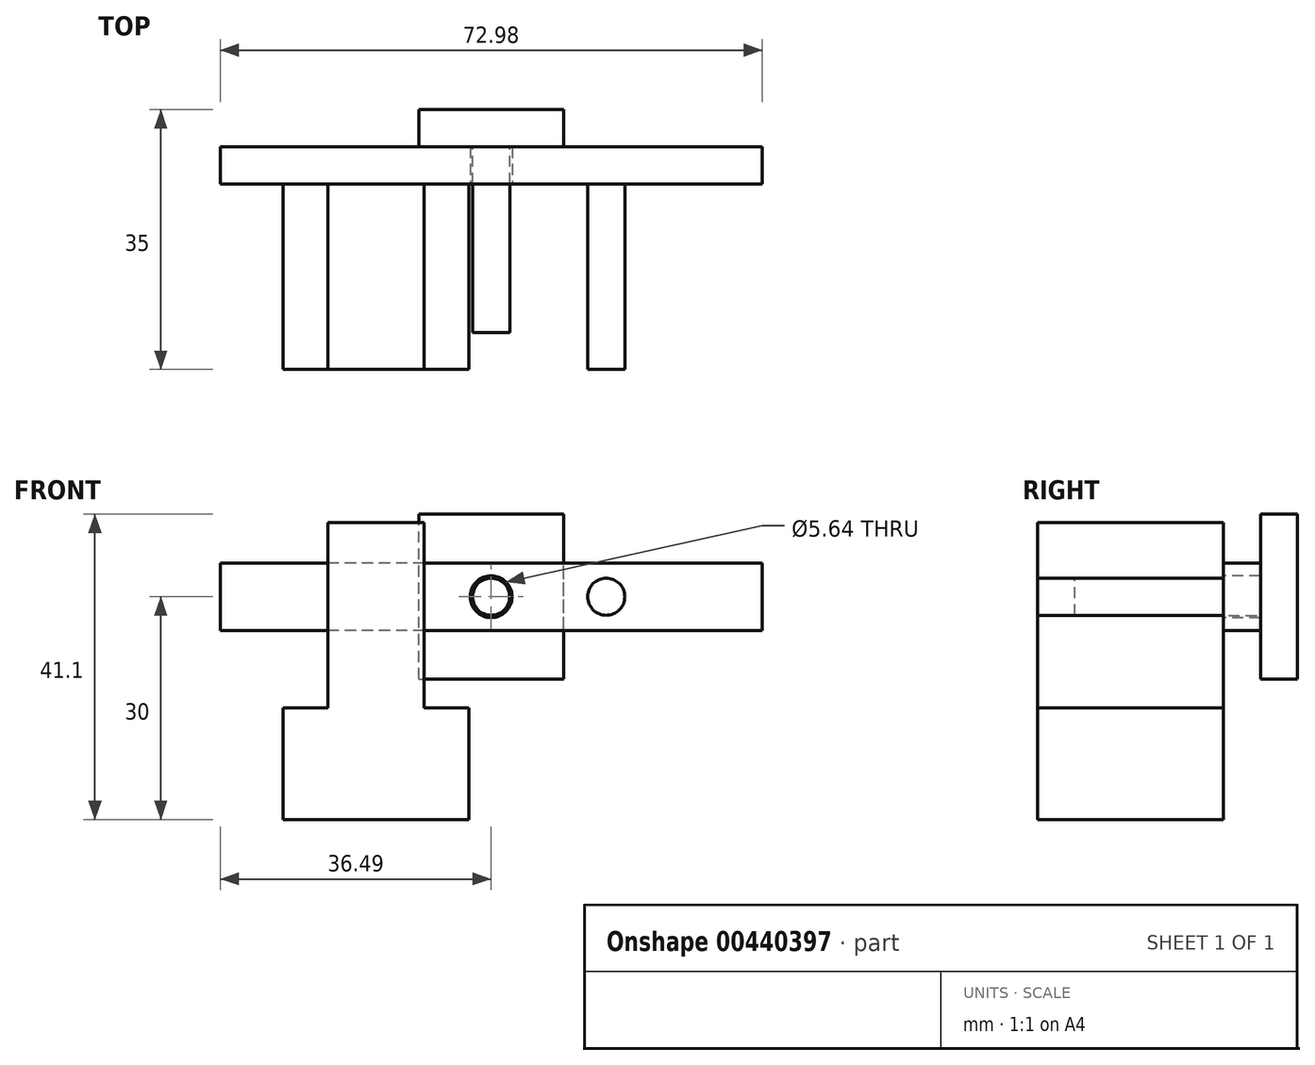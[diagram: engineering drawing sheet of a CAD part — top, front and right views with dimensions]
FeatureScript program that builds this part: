
annotation { "Feature Type Name" : "Feature", "Feature Type Description" : "" }
export const myFeature = defineFeature(function(context is Context, id is Id, definition is map)
    precondition{}
    {
        {
            var Q0;
            Q0=qCreatedBy(makeId("Front.planeOp"),FACE);
            var sketch = newSketch(context, id + "F0", { "sketchPlane" : qUnion([Q0])});
            skLineSegment(sketch, "E0.bottom", {"start": v(-28, 0) * mm, "end": v(-3, 0) * mm});
            skLineSegment(sketch, "E0.top", {"start": v(-28, -30) * mm, "end": v(-3, -30) * mm});
            skLineSegment(sketch, "E0.left", {"start": v(-28, 0) * mm, "end": v(-28, -30) * mm});
            skLineSegment(sketch, "E0.right", {"start": v(-3, 0) * mm, "end": v(-3, -30) * mm});
            skSolve(sketch);
        }
        {
            var Q0;
            Q0 = qSketchRegion(id + "F0", true);
            extrude(context, id + "F1", {"entities" : qUnion([Q0]), "depth" : 25 * mm});
        }
        {
            var Q0;
            Q0=makeQuery(id+"F1.opExtrude","SWEPT_FACE",FACE,{"disambiguationData":[OSD([sQuery(id+"F0.wireOp",EDGE,"E0.bottom")])]});
            extrude(context, id + "F2", {"entities" : qUnion([Q0]), "operationType" : NewBodyOperationType.ADD, "depth" : 10 * mm});
        }
        {
            var Q0;
            {var subQ0=sQuery(id+"F0.wireOp",EDGE,"E0.bottom");Q0=makeQuery(id+"F2.boolean.opBoolean","MERGE",FACE,{"derivedFrom":[makeQuery(id+"F1.opExtrude","CAP_FACE",FACE,{"disambiguationData":[OSD([subQ0,sQuery(id+"F0.wireOp",EDGE,"E0.top"),sQuery(id+"F0.wireOp",EDGE,"E0.left"),sQuery(id+"F0.wireOp",EDGE,"E0.right")])],"isStart":false}),makeQuery(id+"F2.opExtrude","SWEPT_FACE",FACE,{"disambiguationData":[OSD([subQ0]),TDD([makeQuery(id+"F1.opExtrude","CAP_EDGE",EDGE,{"disambiguationData":[OSD([subQ0])],"isStart":false})])]})]});}
            var sketch = newSketch(context, id + "F3", { "sketchPlane" : qUnion([Q0])});
            skLineSegment(sketch, "E1", {"start": v(-15.5, 10) * mm, "end": v(-15.5, -13.59) * mm, "construction": true});
            skCircle(sketch, "E2", {"center": v(-15.5, 0) * mm, "radius": 2.5 * mm});
            skSolve(sketch);
        }
        {
            var Q0;
            Q0 = qSketchRegion(id + "F3", true);
            extrude(context, id + "F4", {"entities" : qUnion([Q0]), "operationType" : NewBodyOperationType.REMOVE, "oppositeDirection" : true, "depth" : 25 * mm});
        }
        {
            var Q0;
            Q0=qCreatedBy(makeId("Front.planeOp"),FACE);
            var sketch = newSketch(context, id + "F5", { "sketchPlane" : qUnion([Q0])});
            skLineSegment(sketch, "E3.bottom", {"start": v(36.49, -4.53) * mm, "end": v(-36.49, -4.53) * mm});
            skLineSegment(sketch, "E3.top", {"start": v(36.49, 4.53) * mm, "end": v(-36.49, 4.53) * mm});
            skLineSegment(sketch, "E3.left", {"start": v(36.49, -4.53) * mm, "end": v(36.49, 4.53) * mm});
            skLineSegment(sketch, "E3.right", {"start": v(-36.49, -4.53) * mm, "end": v(-36.49, 4.53) * mm});
            skPoint(sketch, "E3.middle", {"position": v(0, 0) * mm});
            skSolve(sketch);
        }
        {
            var Q0;
            Q0 = qSketchRegion(id + "F5", true);
            extrude(context, id + "F6", {"entities" : qUnion([Q0]), "oppositeDirection" : true, "depth" : 5 * mm});
        }
        {
            var Q0;
            Q0=makeQuery(id+"F6.opExtrude","CAP_FACE",FACE,{"disambiguationData":[OSD([sQuery(id+"F5.wireOp",EDGE,"E3.bottom"),sQuery(id+"F5.wireOp",EDGE,"E3.top"),sQuery(id+"F5.wireOp",EDGE,"E3.left"),sQuery(id+"F5.wireOp",EDGE,"E3.right")])],"isStart":true});
            var sketch = newSketch(context, id + "F7", { "sketchPlane" : qUnion([Q0])});
            skCircle(sketch, "E4", {"center": v(-15.5, 0) * mm, "radius": 2.5 * mm});
            skCircle(sketch, "E5.MirrorC", {"center": v(15.5, 0) * mm, "radius": 2.5 * mm});
            skSolve(sketch);
        }
        {
            var Q0;
            Q0 = qSketchRegion(id + "F7", true);
            extrude(context, id + "F8", {"entities" : qUnion([Q0]), "operationType" : NewBodyOperationType.ADD, "depth" : 25 * mm});
        }
        {
            var Q0;
            Q0=makeQuery(id+"F6.opExtrude","CAP_FACE",FACE,{"disambiguationData":[OSD([sQuery(id+"F5.wireOp",EDGE,"E3.bottom"),sQuery(id+"F5.wireOp",EDGE,"E3.top"),sQuery(id+"F5.wireOp",EDGE,"E3.left"),sQuery(id+"F5.wireOp",EDGE,"E3.right")])],"isStart":true});
            var sketch = newSketch(context, id + "F9", { "sketchPlane" : qUnion([Q0])});
            skCircle(sketch, "E6", {"center": v(0, 0) * mm, "radius": 2.82 * mm});
            skSolve(sketch);
        }
        {
            var Q0;
            Q0 = qSketchRegion(id + "F9", true);
            extrude(context, id + "F10", {"entities" : qUnion([Q0]), "operationType" : NewBodyOperationType.REMOVE, "oppositeDirection" : true, "depth" : 25 * mm});
        }
        {
            var Q0;
            Q0=makeQuery(id+"F6.opExtrude","CAP_FACE",FACE,{"disambiguationData":[OSD([sQuery(id+"F5.wireOp",EDGE,"E3.bottom"),sQuery(id+"F5.wireOp",EDGE,"E3.top"),sQuery(id+"F5.wireOp",EDGE,"E3.left"),sQuery(id+"F5.wireOp",EDGE,"E3.right")])],"isStart":false});
            var sketch = newSketch(context, id + "F11", { "sketchPlane" : qUnion([Q0])});
            skLineSegment(sketch, "E7.bottom", {"start": v(9.76, -11.1) * mm, "end": v(-9.76, -11.1) * mm});
            skLineSegment(sketch, "E7.top", {"start": v(9.76, 11.1) * mm, "end": v(-9.76, 11.1) * mm});
            skLineSegment(sketch, "E7.left", {"start": v(9.76, -11.1) * mm, "end": v(9.76, 11.1) * mm});
            skLineSegment(sketch, "E7.right", {"start": v(-9.76, -11.1) * mm, "end": v(-9.76, 11.1) * mm});
            skPoint(sketch, "E7.middle", {"position": v(0, 0) * mm});
            skSolve(sketch);
        }
        {
            var Q0;
            Q0 = qSketchRegion(id + "F11", true);
            extrude(context, id + "F12", {"entities" : qUnion([Q0]), "depth" : 5 * mm});
        }
        {
            var Q0;
            Q0=makeQuery(id+"F12.opExtrude","CAP_FACE",FACE,{"disambiguationData":[OSD([sQuery(id+"F11.wireOp",EDGE,"E7.bottom"),sQuery(id+"F11.wireOp",EDGE,"E7.top"),sQuery(id+"F11.wireOp",EDGE,"E7.left"),sQuery(id+"F11.wireOp",EDGE,"E7.right")])],"isStart":true});
            var sketch = newSketch(context, id + "F13", { "sketchPlane" : qUnion([Q0])});
            skCircle(sketch, "E8", {"center": v(0, 0) * mm, "radius": 2.5 * mm});
            skSolve(sketch);
        }
        {
            var Q0;
            Q0 = qSketchRegion(id + "F13", true);
            extrude(context, id + "F14", {"entities" : qUnion([Q0]), "operationType" : NewBodyOperationType.ADD, "depth" : 25 * mm});
        }
        {
            var Q0;
            {var subQ0=sQuery(id+"F0.wireOp",EDGE,"E0.bottom");Q0=makeQuery(id+"F2.boolean.opBoolean","MERGE",FACE,{"derivedFrom":[makeQuery(id+"F1.opExtrude","CAP_FACE",FACE,{"disambiguationData":[OSD([subQ0,sQuery(id+"F0.wireOp",EDGE,"E0.top"),sQuery(id+"F0.wireOp",EDGE,"E0.left"),sQuery(id+"F0.wireOp",EDGE,"E0.right")])],"isStart":false}),makeQuery(id+"F2.opExtrude","SWEPT_FACE",FACE,{"disambiguationData":[OSD([subQ0]),TDD([makeQuery(id+"F1.opExtrude","CAP_EDGE",EDGE,{"disambiguationData":[OSD([subQ0])],"isStart":false})])]})]});}
            var sketch = newSketch(context, id + "F15", { "sketchPlane" : qUnion([Q0])});
            skLineSegment(sketch, "E9.bottom", {"start": v(-28, 10) * mm, "end": v(-22, 10) * mm});
            skLineSegment(sketch, "E9.top", {"start": v(-28, -15) * mm, "end": v(-22, -15) * mm});
            skLineSegment(sketch, "E9.left", {"start": v(-28, 10) * mm, "end": v(-28, -15) * mm});
            skLineSegment(sketch, "E9.right", {"start": v(-22, 10) * mm, "end": v(-22, -15) * mm});
            skLineSegment(sketch, "E10.bottom", {"start": v(-3, 10) * mm, "end": v(-9, 10) * mm});
            skLineSegment(sketch, "E10.top", {"start": v(-3, -15) * mm, "end": v(-9, -15) * mm});
            skLineSegment(sketch, "E10.left", {"start": v(-3, 10) * mm, "end": v(-3, -15) * mm});
            skLineSegment(sketch, "E10.right", {"start": v(-9, 10) * mm, "end": v(-9, -15) * mm});
            skSolve(sketch);
        }
        {
            var Q0;
            Q0 = qSketchRegion(id + "F15", true);
            extrude(context, id + "F16", {"entities" : qUnion([Q0]), "operationType" : NewBodyOperationType.REMOVE, "oppositeDirection" : true, "depth" : 25 * mm});
        }
    });
